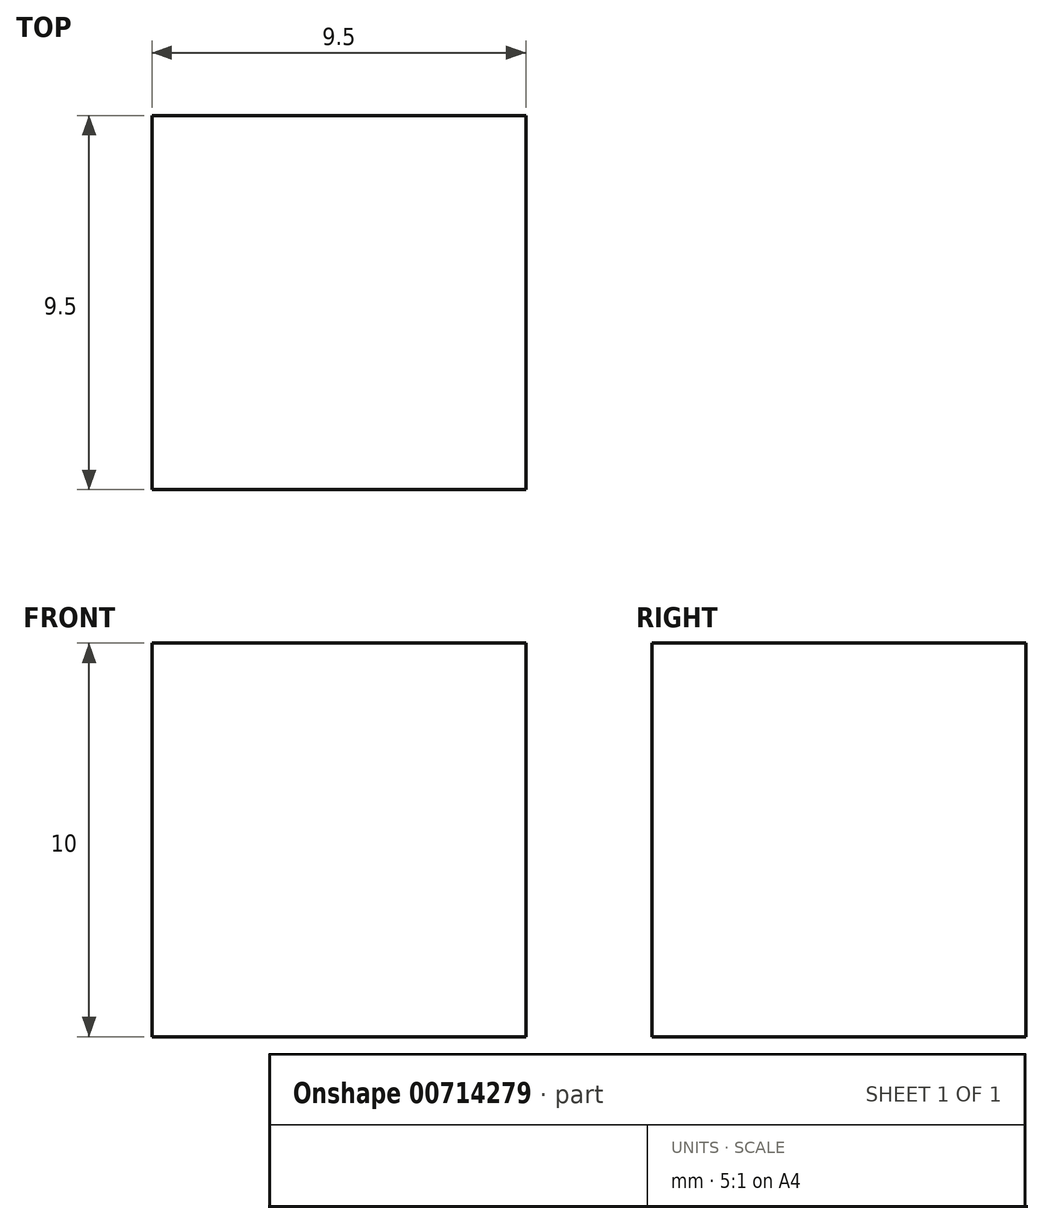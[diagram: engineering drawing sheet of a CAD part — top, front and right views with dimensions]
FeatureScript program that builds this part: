
annotation { "Feature Type Name" : "Feature", "Feature Type Description" : "" }
export const myFeature = defineFeature(function(context is Context, id is Id, definition is map)
    precondition{}
    {
        {
            var Q0;
            Q0=qCreatedBy(makeId("Top.planeOp"),FACE);
            var sketch = newSketch(context, id + "F0", { "sketchPlane" : qUnion([Q0])});
            skLineSegment(sketch, "E0.bottom", {"start": v(-4.75, 4.75) * mm, "end": v(4.75, 4.75) * mm});
            skLineSegment(sketch, "E0.top", {"start": v(-4.75, -4.75) * mm, "end": v(4.75, -4.75) * mm});
            skLineSegment(sketch, "E0.left", {"start": v(-4.75, 4.75) * mm, "end": v(-4.75, -4.75) * mm});
            skLineSegment(sketch, "E0.right", {"start": v(4.75, 4.75) * mm, "end": v(4.75, -4.75) * mm});
            skLineSegment(sketch, "E1", {"start": v(-4.75, -4.75) * mm, "end": v(4.75, 4.75) * mm, "construction": true});
            skSolve(sketch);
        }
        {
            var Q0;
            Q0=makeQuery(id+"F0.imprint","IMPRINT",FACE,{"disambiguationData":[TD([[makeQuery(id+"F0.imprint","IMPRINT",EDGE,{"derivedFrom":sQuery(id+"F0.wireOp",EDGE,"E0.bottom")}),-1.0]])]});
            extrude(context, id + "F1", {"entities" : qUnion([Q0]), "endBound" : BoundingType.SYMMETRIC, "depth" : 10 * mm, "offsetDistance" : 25 * mm});
        }
    });
